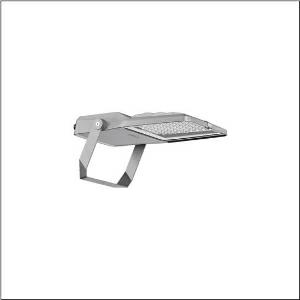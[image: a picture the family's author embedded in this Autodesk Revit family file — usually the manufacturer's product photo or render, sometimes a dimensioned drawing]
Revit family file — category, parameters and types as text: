
# Revit family: floodlight_fl_21_mini___pl52_5xa7776b2d1a_de24
name_source: partatom
category: Lighting Fixtures
units: mm (PartAtom-declared; Revit-internal decimal feet)

## family parameters
Cut with Voids When Loaded = No
Host = Face
Light Source = No
Part Type = Normal
Room Calculation Point = No
Round Connector Dimension = Use Diameter
Shared = No

## types (1)
- --- (1 x LED, 6230 lm, 45.7 W, 3000K)
    Apparent Load = 46 VA
    CIE Flux Codes = 26 60 98 100 100
    Color Rendering = 70
    Color Temperature = 3000K
    Default Elevation = 1800 mm
    Description = Floodlight FL 21 mini, floodlight, primary light control with lens, of PMMA, primary optical cover: protective disc, of toughened safety glass, transparent, light distribution: PL52, light emission: direct distribution, installation type: surface-mounted, LED, High Power LED, rated luminous flux: 6.230lm, luminous efficacy: 136lm/W, light colour: 730, colour temperature: 3000K, control gear: ECG Smart Interface, control: flexible luminous flux parameterisation, time-dependent luminous flux control, constant luminous flux control, overheat protection, presetting dimming logarithmic, with terminal, 6-pole, mains connection: 220..240V, AC, 50/60Hz, start of lifetime: 46W, end of lifetime: 48W, reduction: 22W, luminaire housing, of diecast aluminium, powder-coated, Siteco® metallic grey (DB 702S), corrosivity category C5 according to DIN EN ISO 12944, mounting bracket, of steel, galvanised, powder-coated, Siteco® metallic grey (DB 702S), protection rating (complete): IP66, insulation class (complete): insulation class II (safety insulation), certification: CE, protection symbol: D, impact resistance: IK08, permissible operating ambient temperature: -40..+40°C, permissible operating ambient temperature for outdoor applications: -40..+50°C, standard: DIN EN 12944, packaging unit: 1 piece

Light Distribution: PL52
    Height = 70 mm
    Lamp = 1 x LED
    Lamp Light Flux = 6230 lm
    Lamp Power = 45.7 W
    Lamp count = 1
    Length = 485 mm
    Luminous efficacy = 136 lm/W
    Manufacturer = Siteco
    ModVariant = No
    Model = 5XA7776B2D1A
    Number of Poles = 1
    OnlyDefault = Yes
    Power Factor = 1
    Product Name = Floodlight FL 21 mini | PL52
    Product group = floodlight | pylon top
    ProductGroupID = 6101
    Protection Class = Protection class II
    Protection Degree = IP 66
    RLX_Detail_Level = 1
    RlxData = <blob elided: 96081 chars, md5=70af5b10>
    Socket = socket
    Standby Power = 0 W
    System Light Flux = 6230 lm
    System Power = 46 W
    Type Comments = factory setting: luminous flux: 100 % | dim-lin: 254 | 463 mA
    Type Image = l_1006845.jpg
    URL = http://relux.com
    VarID = @adj_074573
    Voltage = 0 V
    Weight = 0.00 kg
    Width = 337 mm

## geometry (parser evidence)
native form markers: Blend x4, Sweep x12
no freeform markers — native parametric forms only
